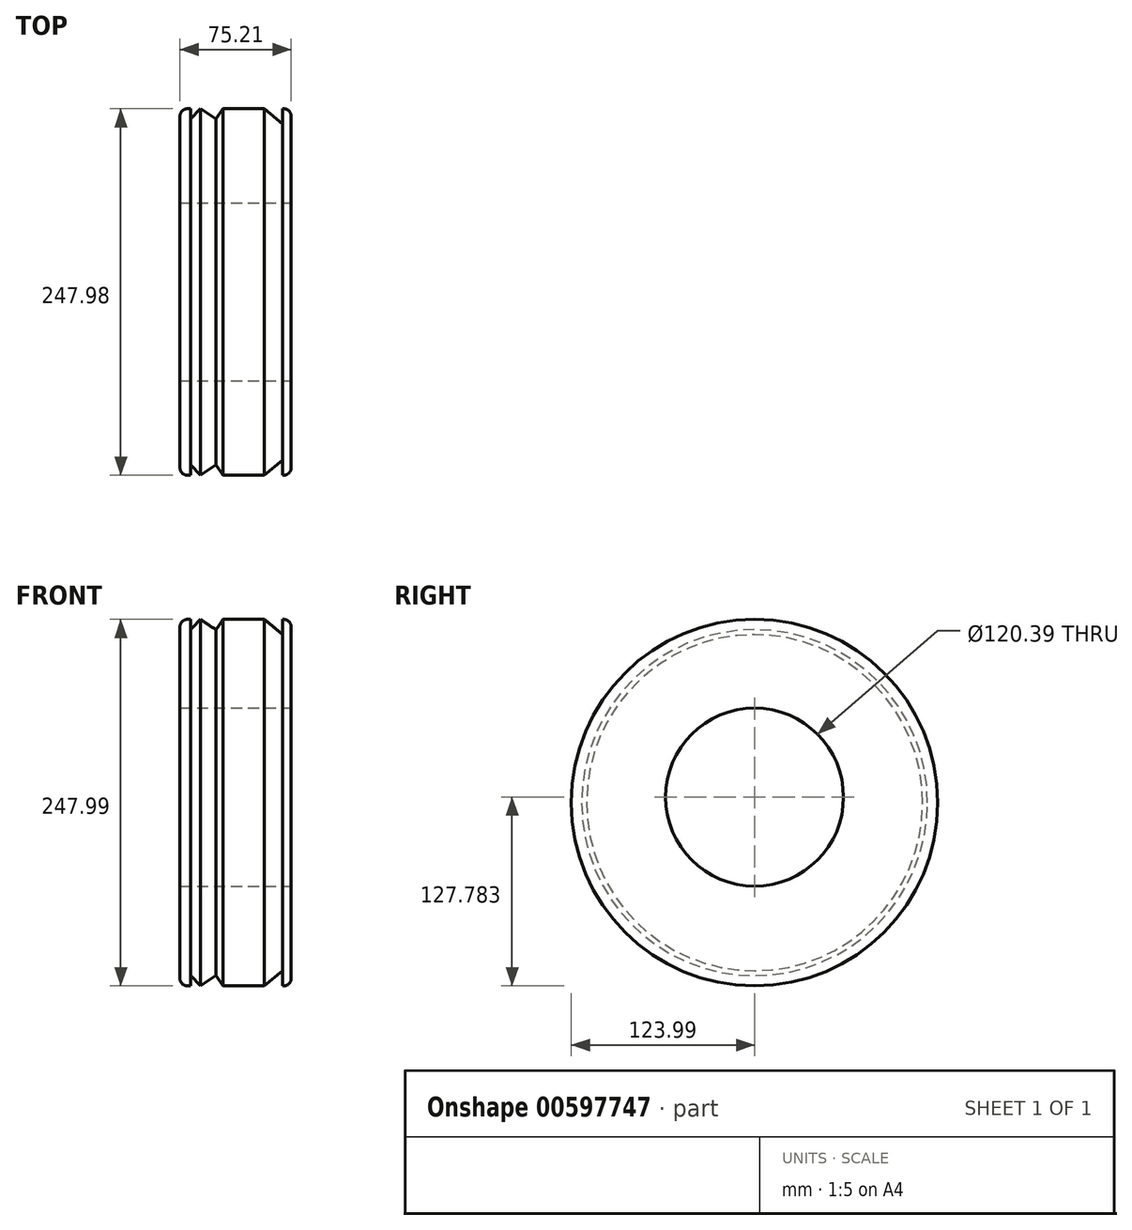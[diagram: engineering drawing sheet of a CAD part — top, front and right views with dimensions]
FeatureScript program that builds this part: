
annotation { "Feature Type Name" : "Feature", "Feature Type Description" : "" }
export const myFeature = defineFeature(function(context is Context, id is Id, definition is map)
    precondition{}
    {
        {
            var Q0;
            Q0=qCreatedBy(makeId("Front.planeOp"),FACE);
            var sketch = newSketch(context, id + "F0", { "sketchPlane" : qUnion([Q0])});
            skLineSegment(sketch, "E0.bottom", {"start": v(-37.34, 56.4) * mm, "end": v(37.87, 56.4) * mm});
            skLineSegment(sketch, "E0.top", {"start": v(-37.34, -67.59) * mm, "end": v(37.87, -67.59) * mm});
            skLineSegment(sketch, "E0.left", {"start": v(-37.34, 56.4) * mm, "end": v(-37.34, -67.59) * mm});
            skLineSegment(sketch, "E0.right", {"start": v(37.87, 56.4) * mm, "end": v(37.87, -67.59) * mm});
            skLineSegment(sketch, "E1", {"start": v(-8.24, -67.59) * mm, "end": v(0, -60.62) * mm, "construction": true});
            skLineSegment(sketch, "E2", {"start": v(0, -60.62) * mm, "end": v(4.48, -67.59) * mm, "construction": true});
            skLineSegment(sketch, "E3", {"start": v(4.48, -67.59) * mm, "end": v(15.33, -60.62) * mm, "construction": true});
            skLineSegment(sketch, "E4", {"start": v(15.33, -60.62) * mm, "end": v(19.81, -67.59) * mm, "construction": true});
            skLineSegment(sketch, "E5", {"start": v(-8.24, -67.59) * mm, "end": v(-12.93, -60.62) * mm});
            skLineSegment(sketch, "E6", {"start": v(-12.93, -60.62) * mm, "end": v(-23.61, -67.59) * mm});
            skLineSegment(sketch, "E7", {"start": v(-23.61, -67.59) * mm, "end": v(-30.12, -60.62) * mm});
            skLineSegment(sketch, "E8", {"start": v(-30.12, -60.62) * mm, "end": v(-30.12, -67.59) * mm});
            skLineSegment(sketch, "E9", {"start": v(19.81, -67.59) * mm, "end": v(32.18, -57.27) * mm});
            skLineSegment(sketch, "E10", {"start": v(32.18, -57.27) * mm, "end": v(32.18, -67.59) * mm});
            skSolve(sketch);
        }
        {
            var Q0;
            Q0=makeQuery(id+"F0.imprint","IMPRINT",FACE,{"disambiguationData":[TD([[makeQuery(id+"F0.imprint","IMPRINT",EDGE,{"derivedFrom":sQuery(id+"F0.wireOp",EDGE,"E0.bottom")}),-1.0]])]});
            var Q1;
            Q1=sQuery(id+"F0.wireOp",EDGE,"E0.bottom");
            revolve(context, id + "F1", {"entities" : qUnion([Q0]), "axis" : qUnion([Q1]), "revolveType" : RevolveType.FULL});
        }
        {
            var Q0;
            Q0=qCreatedBy(makeId("Right.planeOp"),FACE);
            var sketch = newSketch(context, id + "F2", { "sketchPlane" : qUnion([Q0])});
            skCircle(sketch, "E11", {"center": v(0, 60.2) * mm, "radius": 60.2 * mm});
            skSolve(sketch);
        }
        {
            var Q0;
            Q0=makeQuery(id+"F2.imprint","IMPRINT",FACE,{"disambiguationData":[TD([[makeQuery(id+"F2.imprint","IMPRINT",EDGE,{"derivedFrom":sQuery(id+"F2.wireOp",EDGE,"E11")}),1.0]])]});
            extrude(context, id + "F3", {"entities" : qUnion([Q0]), "operationType" : NewBodyOperationType.REMOVE, "endBound" : BoundingType.SYMMETRIC, "oppositeDirection" : true, "depth" : 2540 * mm, "offsetDistance" : 25.4 * mm});
        }
        {
            var Q0;
            Q0=makeQuery(id+"F1.opRevolve","SWEPT_EDGE",EDGE,{"disambiguationData":[OSD([sQuery(id+"F0.wireOp",EDGE,"E0.top"),sQuery(id+"F0.wireOp",EDGE,"E0.right")])]});
            var Q1;
            Q1=makeQuery(id+"F1.opRevolve","SWEPT_EDGE",EDGE,{"disambiguationData":[OSD([sQuery(id+"F0.wireOp",EDGE,"E0.top"),sQuery(id+"F0.wireOp",EDGE,"E0.left")])]});
            fillet(context, id + "F4", {"entities" : qUnion([Q0, Q1]), "radius" : 5.08 * mm, "tangentPropagation" : true, "allowEdgeOverflow" : false});
        }
    });
